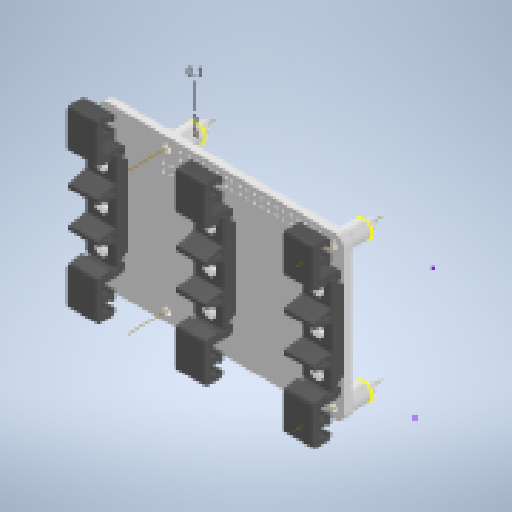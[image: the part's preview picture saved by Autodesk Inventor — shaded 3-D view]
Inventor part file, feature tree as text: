
AUTODESK INVENTOR PART (.ipt)
format: ipt  version: 2023 (Build 270158030, 158C)  size: 1,203,712 bytes
history: native  units: mm
features: other x23, reference x14, extrude x9, sketch x6, fillet x2, pattern_linear x2, chamfer x1, projected_geometry x1
ambient origin geometry x8: Origin, YZ Plane, XZ Plane, XY Plane, X Axis, Y Axis, Z Axis, Center Point
bodies: Solid4 (feature_tree), Solid5 (feature_tree)
feature tree (58):
  other  "backplate"
  other  "Blocks"
  extrude  "Extrusion1"  Depth=10.0mm TaperAngle=0.0deg
  extrude  "Extrusion2"  Depth=10.0mm TaperAngle=0.0deg
  extrude  "Extrusion3"  Depth=2.0mm TaperAngle=0.0deg
  fillet  "Fillet4"  Radius=4.0mm
  extrude  "Extrusion4"  Depth=2.5mm TaperAngle=0.0deg
  extrude  "Extrusion5"  Depth=1.759846mm
  other  "Work Axis10"
  other  "Work Axis11"
  other  "Work Axis12"
  other  "Work Axis13"
  extrude  "Extrusion6"  Depth=2.0mm
  fillet  "Fillet6"  Radius=0.1mm
  extrude  "Extrusion8"  Depth=2.0mm
  chamfer  "Chamfer1"  Distance=0.5mm
  extrude  "Extrusion9"  Depth=2.0mm
  extrude  "Extrusion10"  Depth=2.0mm
  pattern_linear  "Rectangular Pattern1"  Spacing1=3.44912mm  [1 undecoded]
  pattern_linear  "Rectangular Pattern2"  Spacing1=5.0mm  [1 undecoded]
  sketch  "Sketch1"  dims[d0=6.2mm d2=10.0mm d3=0.0mm]
  reference  "Reference2"
  sketch  "Sketch2"  dims[d4=2.5mm d5=0.0mm d9=10.0mm d10=0.0mm]
  other  "din-rail-clip-outline"
  projected_geometry  "Projected Loop1"
  sketch  "Sketch6"  dims[d12=2.0mm d16=2.0mm d17=0.0mm d18=4.0mm d19=0.785398mm]
  other  "crosscut"
  other  "Block3"
  reference  "Reference8"
  reference  "Reference9"
  reference  "Reference10"
  reference  "Reference11"
  reference  "Reference12"
  reference  "Reference13"
  reference  "Reference14"
  reference  "Reference15"
  reference  "Reference16"
  reference  "Reference17"
  reference  "Reference18"
  reference  "Reference19"
  reference  "Reference20"
  other  "DIN-rail-clip-long"
  sketch  "Sketch8"  dims[d21=0.4mm d25=2.5mm d26=0.0mm]
  sketch  "Sketch9"  dims[d27=1.0mm d30=1.759846mm]
  sketch  "Sketch10"  dims[d31=1.271846mm d32=3.0mm d40=0.1mm d41=0.2mm d42=0.5mm d43=3.1mm d44=3.4mm d46=3.44912mm d47=5.0mm d48=5.0mm d50=6.850895mm d51=6.850895mm d52=13.701789mm d53=0.0mm d54=0.0mm d55=1.0mm d56=2.0mm d57=45.0deg d58=0.0mm d59=0.0mm d60=5.47mm d61=2.0mm d62=0.0mm d63=30.0mm d65=75.0mm d66=30.0mm d68=75.0mm d69=2.0mm d70=2.0mm d74=2.6192mm d75=4.0mm d77=4.0mm d78=0.75mm d79=1.5mm d80=2.0mm d82=1.0mm d28=0.5mm d29=0.872665mm]
  other  "Pattern of DIN-rail-clip-long:1"
  other  "Pattern of DIN-rail-clip-long:2"
  other  "arduino-DIN-mount.iam"
  other  "arduinoMegaDetailed:1"
  other  "crosscut:1"
  other  "crosscut:2"
  other  "crosscut:3"
  other  "crosscut:5"
  other  "Block3:1"
  other  "raspi-DIN-mount.iam"
  other  "Raspberry Pi 4 Model B:1"
  other  "PCB, RPi4ModelB_1"
  other  "Block3:2"
note: 2 required parameter values undecoded (feature->parameter linkage not recoverable at this tier; creation-order binding heuristic only, values carry confidence <= 0.55)
